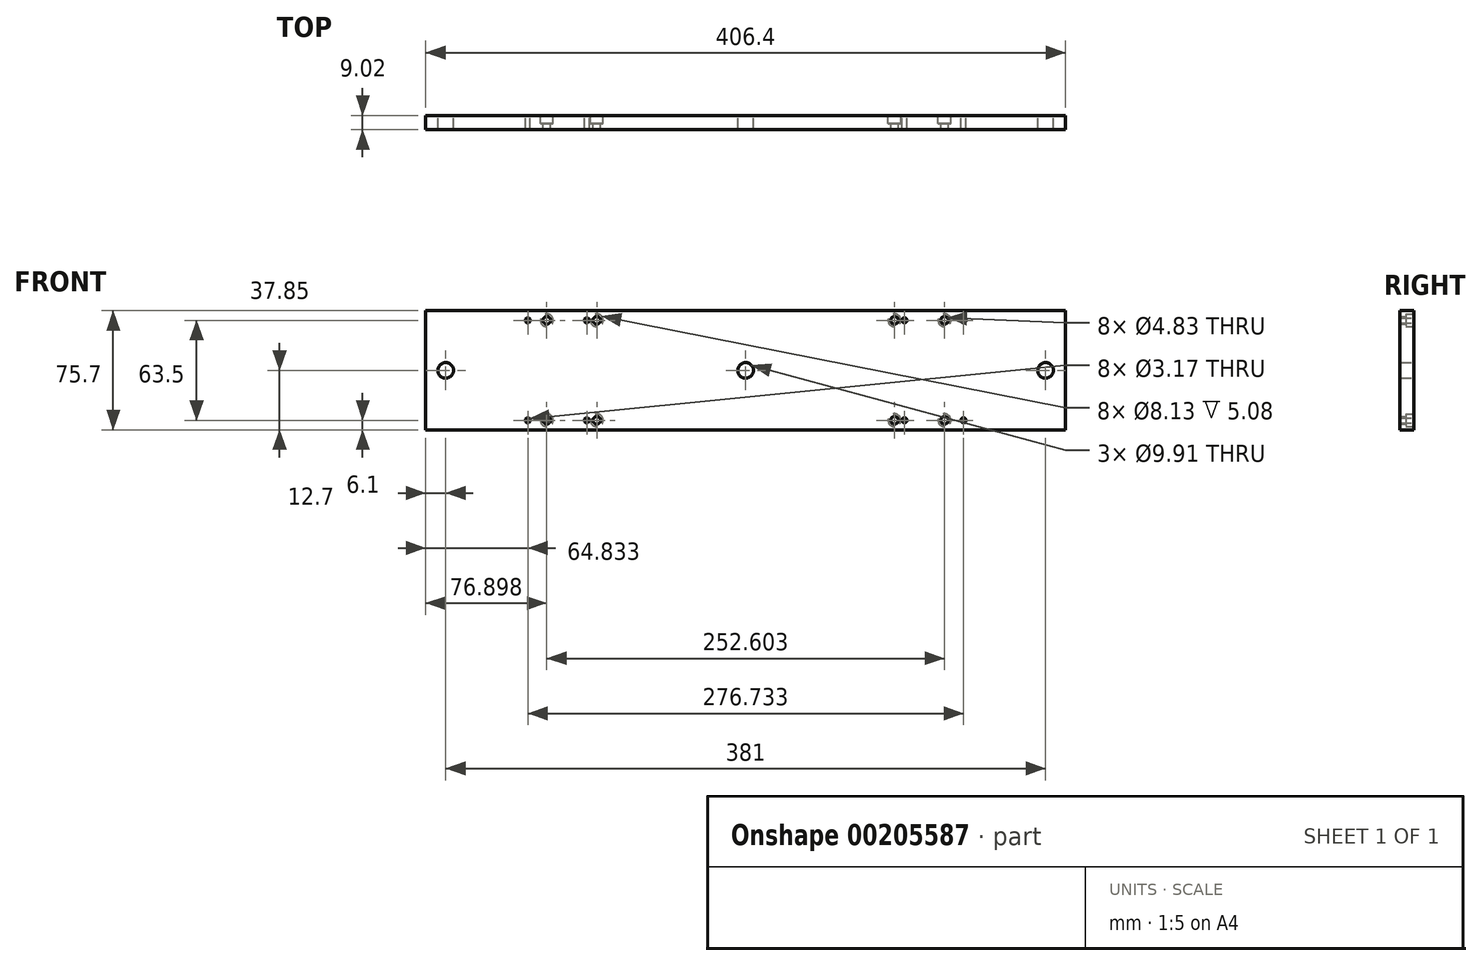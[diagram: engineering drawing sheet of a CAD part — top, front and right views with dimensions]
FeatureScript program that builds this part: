
annotation { "Feature Type Name" : "Feature", "Feature Type Description" : "" }
export const myFeature = defineFeature(function(context is Context, id is Id, definition is map)
    precondition{}
    {
        {
            var Q0;
            Q0=qCreatedBy(makeId("Front.planeOp"),FACE);
            var sketch = newSketch(context, id + "F0", { "sketchPlane" : qUnion([Q0])});
            skLineSegment(sketch, "E0.bottom", {"start": v(-203.2, 37.85) * mm, "end": v(203.2, 37.85) * mm});
            skLineSegment(sketch, "E0.top", {"start": v(-203.2, -37.85) * mm, "end": v(203.2, -37.85) * mm});
            skLineSegment(sketch, "E0.left", {"start": v(-203.2, 37.85) * mm, "end": v(-203.2, -37.85) * mm});
            skLineSegment(sketch, "E0.right", {"start": v(203.2, 37.85) * mm, "end": v(203.2, -37.85) * mm});
            skPoint(sketch, "E0.middle", {"position": v(0, 0) * mm});
            skCircle(sketch, "E1", {"center": v(-138.37, 31.75) * mm, "radius": 1.59 * mm});
            skCircle(sketch, "E2", {"center": v(-126.3, 31.75) * mm, "radius": 2.41 * mm});
            skCircle(sketch, "E3", {"center": v(-100.9, 31.75) * mm, "radius": 1.59 * mm});
            skCircle(sketch, "E4", {"center": v(-94.55, 31.75) * mm, "radius": 2.41 * mm});
            skCircle(sketch, "E5.MirrorC", {"center": v(-94.55, -31.75) * mm, "radius": 2.41 * mm});
            skCircle(sketch, "E6.MirrorC", {"center": v(-100.9, -31.75) * mm, "radius": 1.59 * mm});
            skCircle(sketch, "E7.MirrorC", {"center": v(-126.3, -31.75) * mm, "radius": 2.41 * mm});
            skCircle(sketch, "E8.MirrorC", {"center": v(-138.37, -31.75) * mm, "radius": 1.59 * mm});
            skCircle(sketch, "E9.MirrorC", {"center": v(138.37, 31.75) * mm, "radius": 1.59 * mm});
            skCircle(sketch, "E10.MirrorC", {"center": v(126.3, 31.75) * mm, "radius": 2.41 * mm});
            skCircle(sketch, "E11.MirrorC", {"center": v(100.9, 31.75) * mm, "radius": 1.59 * mm});
            skCircle(sketch, "E12.MirrorC", {"center": v(94.55, 31.75) * mm, "radius": 2.41 * mm});
            skCircle(sketch, "E13.MirrorC", {"center": v(94.55, -31.75) * mm, "radius": 2.41 * mm});
            skCircle(sketch, "E14.MirrorC", {"center": v(138.37, -31.75) * mm, "radius": 1.59 * mm});
            skCircle(sketch, "E15.MirrorC", {"center": v(126.3, -31.75) * mm, "radius": 2.41 * mm});
            skCircle(sketch, "E16.MirrorC", {"center": v(100.9, -31.75) * mm, "radius": 1.59 * mm});
            skCircle(sketch, "E17", {"center": v(0, 0) * mm, "radius": 4.95 * mm});
            skCircle(sketch, "E18", {"center": v(190.5, 0) * mm, "radius": 4.95 * mm});
            skCircle(sketch, "E19", {"center": v(-190.5, 0) * mm, "radius": 4.95 * mm});
            skSolve(sketch);
        }
        {
            var Q0;
            Q0=qSketchRegion(id+"F0",true);
            extrude(context, id + "F1", {"entities" : qUnion([Q0]), "depth" : 9.02 * mm});
        }
        {
            var Q0;
            Q0=makeQuery(id+"F1.opExtrude","CAP_FACE",FACE,{"disambiguationData":[OSD([sQuery(id+"F0.wireOp",EDGE,"E0.bottom"),sQuery(id+"F0.wireOp",EDGE,"E0.top"),sQuery(id+"F0.wireOp",EDGE,"E0.left"),sQuery(id+"F0.wireOp",EDGE,"E0.right"),sQuery(id+"F0.wireOp",EDGE,"E1"),sQuery(id+"F0.wireOp",EDGE,"E2"),sQuery(id+"F0.wireOp",EDGE,"E3"),sQuery(id+"F0.wireOp",EDGE,"E4"),sQuery(id+"F0.wireOp",EDGE,"E5.MirrorC"),sQuery(id+"F0.wireOp",EDGE,"E6.MirrorC"),sQuery(id+"F0.wireOp",EDGE,"E7.MirrorC"),sQuery(id+"F0.wireOp",EDGE,"E8.MirrorC"),sQuery(id+"F0.wireOp",EDGE,"E9.MirrorC"),sQuery(id+"F0.wireOp",EDGE,"E10.MirrorC"),sQuery(id+"F0.wireOp",EDGE,"E11.MirrorC"),sQuery(id+"F0.wireOp",EDGE,"E12.MirrorC"),sQuery(id+"F0.wireOp",EDGE,"E13.MirrorC"),sQuery(id+"F0.wireOp",EDGE,"E14.MirrorC"),sQuery(id+"F0.wireOp",EDGE,"E15.MirrorC"),sQuery(id+"F0.wireOp",EDGE,"E16.MirrorC"),sQuery(id+"F0.wireOp",EDGE,"E17"),sQuery(id+"F0.wireOp",EDGE,"E18"),sQuery(id+"F0.wireOp",EDGE,"E19")])],"isStart":true});
            var sketch = newSketch(context, id + "F2", { "sketchPlane" : qUnion([Q0])});
            skCircle(sketch, "E20", {"center": v(126.3, 31.75) * mm, "radius": 4.06 * mm});
            skCircle(sketch, "E21", {"center": v(94.55, 31.75) * mm, "radius": 4.06 * mm});
            skCircle(sketch, "E22", {"center": v(126.3, -31.75) * mm, "radius": 4.06 * mm});
            skCircle(sketch, "E23", {"center": v(94.55, -31.75) * mm, "radius": 4.06 * mm});
            skCircle(sketch, "E24", {"center": v(-126.3, 31.75) * mm, "radius": 4.06 * mm});
            skCircle(sketch, "E25", {"center": v(-94.55, 31.75) * mm, "radius": 4.06 * mm});
            skCircle(sketch, "E26", {"center": v(-94.55, -31.75) * mm, "radius": 4.06 * mm});
            skCircle(sketch, "E27", {"center": v(-126.3, -31.75) * mm, "radius": 4.06 * mm});
            skSolve(sketch);
        }
        {
            var Q0;
            Q0=qSketchRegion(id+"F2",true);
            extrude(context, id + "F3", {"entities" : qUnion([Q0]), "operationType" : NewBodyOperationType.REMOVE, "oppositeDirection" : true, "depth" : 5.08 * mm});
        }
    });
